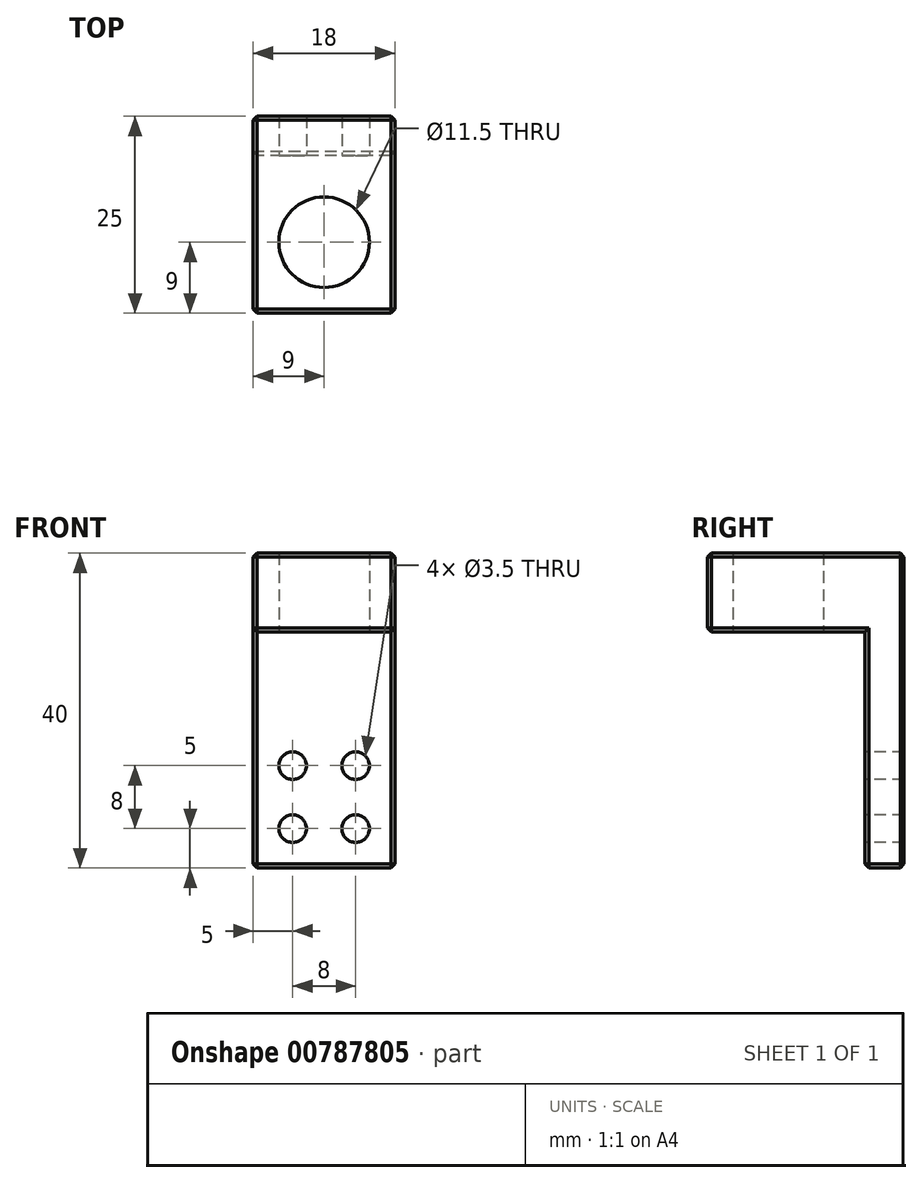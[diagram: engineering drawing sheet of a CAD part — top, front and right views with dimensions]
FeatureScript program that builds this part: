
annotation { "Feature Type Name" : "Feature", "Feature Type Description" : "" }
export const myFeature = defineFeature(function(context is Context, id is Id, definition is map)
    precondition{}
    {
        {
            var Q0;
            Q0=qCreatedBy(makeId("Front.planeOp"),FACE);
            var sketch = newSketch(context, id + "F0", { "sketchPlane" : qUnion([Q0])});
            skLineSegment(sketch, "E0.bottom", {"start": v(9, 20) * mm, "end": v(-9, 20) * mm});
            skLineSegment(sketch, "E0.top", {"start": v(9, -20) * mm, "end": v(-9, -20) * mm});
            skLineSegment(sketch, "E0.left", {"start": v(9, 20) * mm, "end": v(9, -20) * mm});
            skLineSegment(sketch, "E0.right", {"start": v(-9, 20) * mm, "end": v(-9, -20) * mm});
            skPoint(sketch, "E0.middle", {"position": v(0, 0) * mm});
            skSolve(sketch);
        }
        {
            var Q0;
            Q0=makeQuery(id+"F0.imprint","IMPRINT",FACE,{"disambiguationData":[TD([[makeQuery(id+"F0.imprint","IMPRINT",EDGE,{"derivedFrom":sQuery(id+"F0.wireOp",EDGE,"E0.bottom")}),1.0]])]});
            extrude(context, id + "F1", {"entities" : qUnion([Q0]), "depth" : 5 * mm, "offsetDistance" : 25 * mm});
        }
        {
            var Q0;
            Q0=makeQuery(id+"F1.opExtrude","CAP_FACE",FACE,{"disambiguationData":[OSD([sQuery(id+"F0.wireOp",EDGE,"E0.bottom"),sQuery(id+"F0.wireOp",EDGE,"E0.top"),sQuery(id+"F0.wireOp",EDGE,"E0.left"),sQuery(id+"F0.wireOp",EDGE,"E0.right")])],"isStart":false});
            var sketch = newSketch(context, id + "F2", { "sketchPlane" : qUnion([Q0])});
            skCircle(sketch, "E1", {"center": v(4, -15) * mm, "radius": 1.75 * mm});
            skCircle(sketch, "E2", {"center": v(-4, -15) * mm, "radius": 1.75 * mm});
            skCircle(sketch, "E3", {"center": v(4, -7) * mm, "radius": 1.75 * mm});
            skCircle(sketch, "E4", {"center": v(-4, -7) * mm, "radius": 1.75 * mm});
            skSolve(sketch);
        }
        {
            var Q0;
            Q0=makeQuery(id+"F2.imprint","IMPRINT",FACE,{"disambiguationData":[TD([[makeQuery(id+"F2.imprint","IMPRINT",EDGE,{"derivedFrom":sQuery(id+"F2.wireOp",EDGE,"E2")}),1.0]])]});
            var Q1;
            Q1=makeQuery(id+"F2.imprint","IMPRINT",FACE,{"disambiguationData":[TD([[makeQuery(id+"F2.imprint","IMPRINT",EDGE,{"derivedFrom":sQuery(id+"F2.wireOp",EDGE,"E1")}),1.0]])]});
            var Q2;
            Q2=makeQuery(id+"F2.imprint","IMPRINT",FACE,{"disambiguationData":[TD([[makeQuery(id+"F2.imprint","IMPRINT",EDGE,{"derivedFrom":sQuery(id+"F2.wireOp",EDGE,"E3")}),1.0]])]});
            var Q3;
            Q3=makeQuery(id+"F2.imprint","IMPRINT",FACE,{"disambiguationData":[TD([[makeQuery(id+"F2.imprint","IMPRINT",EDGE,{"derivedFrom":sQuery(id+"F2.wireOp",EDGE,"E4")}),1.0]])]});
            extrude(context, id + "F3", {"entities" : qUnion([Q0, Q1, Q2, Q3]), "operationType" : NewBodyOperationType.REMOVE, "endBound" : BoundingType.UP_TO_NEXT, "oppositeDirection" : true, "depth" : 25 * mm, "offsetDistance" : 25 * mm});
        }
        {
            var Q0;
            Q0=makeQuery(id+"F1.opExtrude","CAP_FACE",FACE,{"disambiguationData":[OSD([sQuery(id+"F0.wireOp",EDGE,"E0.bottom"),sQuery(id+"F0.wireOp",EDGE,"E0.top"),sQuery(id+"F0.wireOp",EDGE,"E0.left"),sQuery(id+"F0.wireOp",EDGE,"E0.right")])],"isStart":false});
            var sketch = newSketch(context, id + "F4", { "sketchPlane" : qUnion([Q0])});
            skLineSegment(sketch, "E5.bottom", {"start": v(9, 20) * mm, "end": v(-9, 20) * mm});
            skLineSegment(sketch, "E5.top", {"start": v(9, 10) * mm, "end": v(-9, 10) * mm});
            skLineSegment(sketch, "E5.left", {"start": v(9, 20) * mm, "end": v(9, 10) * mm});
            skLineSegment(sketch, "E5.right", {"start": v(-9, 20) * mm, "end": v(-9, 10) * mm});
            skSolve(sketch);
        }
        {
            var Q0;
            Q0=makeQuery(id+"F4.imprint","IMPRINT",FACE,{"disambiguationData":[TD([[makeQuery(id+"F4.imprint","IMPRINT",EDGE,{"derivedFrom":sQuery(id+"F4.wireOp",EDGE,"E5.bottom")}),1.0]])]});
            extrude(context, id + "F5", {"entities" : qUnion([Q0]), "operationType" : NewBodyOperationType.ADD, "depth" : 20 * mm, "offsetDistance" : 25 * mm});
        }
        {
            var Q0;
            Q0=makeQuery(id+"F5.opExtrude","SWEPT_FACE",FACE,{"disambiguationData":[OSD([sQuery(id+"F4.wireOp",EDGE,"E5.top")])]});
            var sketch = newSketch(context, id + "F6", { "sketchPlane" : qUnion([Q0])});
            skCircle(sketch, "E6", {"center": v(0, 16) * mm, "radius": 5.75 * mm});
            skPoint(sketch, "E6.centerSnap0", {"position": v(0, 25) * mm});
            skSolve(sketch);
        }
        {
            var Q0;
            Q0=makeQuery(id+"F6.imprint","IMPRINT",FACE,{"disambiguationData":[TD([[makeQuery(id+"F6.imprint","IMPRINT",EDGE,{"derivedFrom":sQuery(id+"F6.wireOp",EDGE,"E6")}),1.0]])]});
            extrude(context, id + "F7", {"entities" : qUnion([Q0]), "operationType" : NewBodyOperationType.REMOVE, "endBound" : BoundingType.UP_TO_NEXT, "oppositeDirection" : true, "depth" : 25 * mm, "offsetDistance" : 25 * mm});
        }
        {
            var Q0;
            Q0=makeQuery(id+"F5.opExtrude","SWEPT_EDGE",EDGE,{"disambiguationData":[OSD([sQuery(id+"F0.wireOp",EDGE,"E0.left"),sQuery(id+"F4.wireOp",EDGE,"E5.top"),sQuery(id+"F4.wireOp",EDGE,"E5.left")])]});
            var Q1;
            Q1=makeQuery(id+"F5.opExtrude","SWEPT_EDGE",EDGE,{"disambiguationData":[OSD([sQuery(id+"F0.wireOp",EDGE,"E0.right"),sQuery(id+"F4.wireOp",EDGE,"E5.top"),sQuery(id+"F4.wireOp",EDGE,"E5.right")])]});
            var Q2;
            Q2=makeQuery(id+"F5.opExtrude","CAP_EDGE",EDGE,{"disambiguationData":[OSD([sQuery(id+"F4.wireOp",EDGE,"E5.top")])],"isStart":false});
            var Q3;
            Q3=makeQuery(id+"F5.opExtrude","CAP_EDGE",EDGE,{"disambiguationData":[OSD([sQuery(id+"F4.wireOp",EDGE,"E5.left")])],"isStart":false});
            var Q4;
            Q4=makeQuery(id+"F5.opExtrude","CAP_EDGE",EDGE,{"disambiguationData":[OSD([sQuery(id+"F4.wireOp",EDGE,"E5.right")])],"isStart":false});
            var Q5;
            Q5=makeQuery(id+"F5.opExtrude","CAP_EDGE",EDGE,{"disambiguationData":[OSD([sQuery(id+"F4.wireOp",EDGE,"E5.bottom")])],"isStart":false});
            var Q6;
            Q6=makeQuery(id+"F5.boolean.opBoolean","MERGE",EDGE,{"derivedFrom":[makeQuery(id+"F1.opExtrude","SWEPT_EDGE",EDGE,{"disambiguationData":[OSD([sQuery(id+"F0.wireOp",EDGE,"E0.bottom"),sQuery(id+"F0.wireOp",EDGE,"E0.left")])]}),makeQuery(id+"F5.opExtrude","SWEPT_EDGE",EDGE,{"disambiguationData":[OSD([sQuery(id+"F4.wireOp",EDGE,"E5.bottom"),sQuery(id+"F4.wireOp",EDGE,"E5.left")])]})]});
            var Q7;
            Q7=makeQuery(id+"F1.opExtrude","CAP_EDGE",EDGE,{"disambiguationData":[OSD([sQuery(id+"F0.wireOp",EDGE,"E0.left")])],"isStart":false});
            var Q8;
            Q8=makeQuery(id+"F1.opExtrude","CAP_EDGE",EDGE,{"disambiguationData":[OSD([sQuery(id+"F0.wireOp",EDGE,"E0.left")])],"isStart":true});
            var Q9;
            Q9=makeQuery(id+"F1.opExtrude","CAP_EDGE",EDGE,{"disambiguationData":[OSD([sQuery(id+"F0.wireOp",EDGE,"E0.top")])],"isStart":true});
            var Q10;
            Q10=makeQuery(id+"F1.opExtrude","SWEPT_EDGE",EDGE,{"disambiguationData":[OSD([sQuery(id+"F0.wireOp",EDGE,"E0.top"),sQuery(id+"F0.wireOp",EDGE,"E0.left")])]});
            var Q11;
            Q11=makeQuery(id+"F1.opExtrude","CAP_EDGE",EDGE,{"disambiguationData":[OSD([sQuery(id+"F0.wireOp",EDGE,"E0.top")])],"isStart":false});
            var Q12;
            Q12=makeQuery(id+"F1.opExtrude","SWEPT_EDGE",EDGE,{"disambiguationData":[OSD([sQuery(id+"F0.wireOp",EDGE,"E0.top"),sQuery(id+"F0.wireOp",EDGE,"E0.right")])]});
            var Q13;
            Q13=makeQuery(id+"F1.opExtrude","CAP_EDGE",EDGE,{"disambiguationData":[OSD([sQuery(id+"F0.wireOp",EDGE,"E0.right")])],"isStart":false});
            var Q14;
            Q14=makeQuery(id+"F1.opExtrude","CAP_EDGE",EDGE,{"disambiguationData":[OSD([sQuery(id+"F0.wireOp",EDGE,"E0.right")])],"isStart":true});
            var Q15;
            Q15=makeQuery(id+"F5.boolean.opBoolean","MERGE",EDGE,{"derivedFrom":[makeQuery(id+"F1.opExtrude","SWEPT_EDGE",EDGE,{"disambiguationData":[OSD([sQuery(id+"F0.wireOp",EDGE,"E0.bottom"),sQuery(id+"F0.wireOp",EDGE,"E0.right")])]}),makeQuery(id+"F5.opExtrude","SWEPT_EDGE",EDGE,{"disambiguationData":[OSD([sQuery(id+"F4.wireOp",EDGE,"E5.bottom"),sQuery(id+"F4.wireOp",EDGE,"E5.right")])]})]});
            var Q16;
            Q16=makeQuery(id+"F1.opExtrude","CAP_EDGE",EDGE,{"disambiguationData":[OSD([sQuery(id+"F0.wireOp",EDGE,"E0.bottom")])],"isStart":true});
            var Q17;
            Q17=makeQuery(id+"F5.opExtrude","CAP_EDGE",EDGE,{"disambiguationData":[OSD([sQuery(id+"F4.wireOp",EDGE,"E5.top")])],"isStart":true});
            var Q18;
            Q18=makeQuery(id+"F7.boolean.opBoolean","COPY",EDGE,{"derivedFrom":makeQuery(id+"F7.opExtrude","CAP_EDGE",EDGE,{"disambiguationData":[OSD([sQuery(id+"F6.wireOp",EDGE,"E6")])],"isStart":true})});
            chamfer(context, id + "F8", {"entities" : qUnion([Q0, Q1, Q2, Q3, Q4, Q5, Q6, Q7, Q8, Q9, Q10, Q11, Q12, Q13, Q14, Q15, Q16, Q17, Q18]), "width" : 0.5 * mm, "tangentPropagation" : true});
        }
    });
